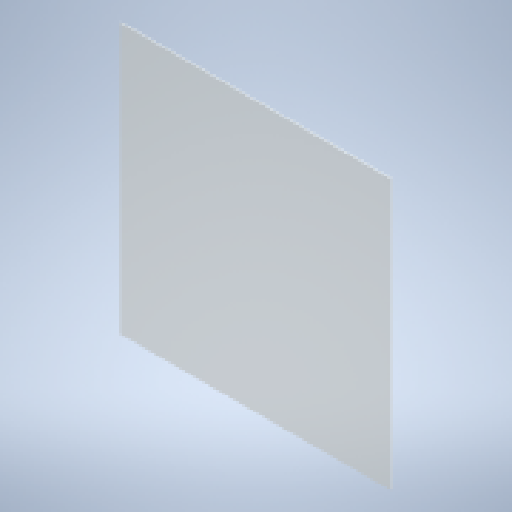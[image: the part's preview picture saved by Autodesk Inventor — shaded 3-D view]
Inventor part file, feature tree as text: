
AUTODESK INVENTOR PART (.ipt)
format: ipt  version: 2025.3 (Build 293356000, 356)  size: 209,920 bytes
history: native  units: mm
features: other x1, extrude x1, sketch x1
ambient origin geometry x8: Origin, YZ Plane, XZ Plane, XY Plane, X Axis, Y Axis, Z Axis, Center Point
bodies: Body1 (feature_tree)
feature tree (3):
  other  "ソリッド1"
  extrude  "押し出し1"  Depth=200.0mm
  sketch  "スケッチ1"
